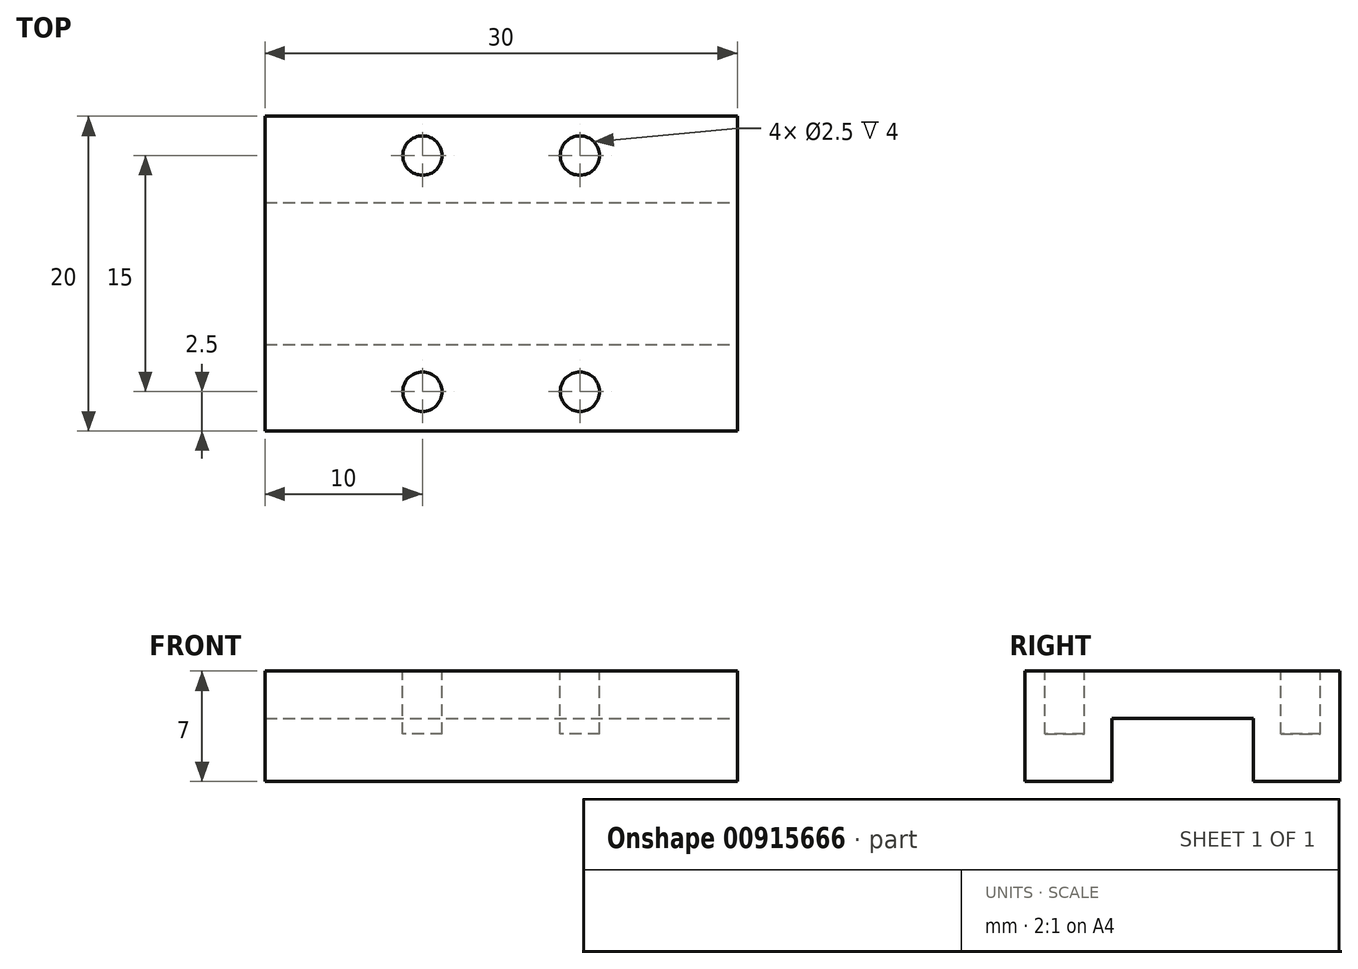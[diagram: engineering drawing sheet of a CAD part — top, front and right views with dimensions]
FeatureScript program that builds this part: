
annotation { "Feature Type Name" : "Feature", "Feature Type Description" : "" }
export const myFeature = defineFeature(function(context is Context, id is Id, definition is map)
    precondition{}
    {
        {
            var Q0;
            Q0=qCreatedBy(makeId("Top.planeOp"),FACE);
            var sketch = newSketch(context, id + "F0", { "sketchPlane" : qUnion([Q0])});
            skLineSegment(sketch, "E0.bottom", {"start": v(-15, 10) * mm, "end": v(15, 10) * mm});
            skLineSegment(sketch, "E0.top", {"start": v(-15, -10) * mm, "end": v(15, -10) * mm});
            skLineSegment(sketch, "E0.left", {"start": v(-15, 10) * mm, "end": v(-15, -10) * mm});
            skLineSegment(sketch, "E0.right", {"start": v(15, 10) * mm, "end": v(15, -10) * mm});
            skSolve(sketch);
        }
        {
            var Q0;
            Q0 = qSketchRegion(id + "F0", true);
            extrude(context, id + "F1", {"entities" : qUnion([Q0]), "depth" : 7 * mm, "offsetDistance" : 25 * mm});
        }
        {
            var Q0;
            Q0=makeQuery(id+"F1.opExtrude","CAP_FACE",FACE,{"disambiguationData":[OSD([sQuery(id+"F0.wireOp",EDGE,"E0.bottom"),sQuery(id+"F0.wireOp",EDGE,"E0.top"),sQuery(id+"F0.wireOp",EDGE,"E0.left"),sQuery(id+"F0.wireOp",EDGE,"E0.right")])],"isStart":false});
            var sketch = newSketch(context, id + "F2", { "sketchPlane" : qUnion([Q0])});
            skLineSegment(sketch, "E1.bottom", {"start": v(-5, 7.5) * mm, "end": v(5, 7.5) * mm, "construction": true});
            skLineSegment(sketch, "E1.top", {"start": v(-5, -7.5) * mm, "end": v(5, -7.5) * mm, "construction": true});
            skLineSegment(sketch, "E1.left", {"start": v(-5, 7.5) * mm, "end": v(-5, -7.5) * mm, "construction": true});
            skLineSegment(sketch, "E1.right", {"start": v(5, 7.5) * mm, "end": v(5, -7.5) * mm, "construction": true});
            skCircle(sketch, "E2", {"center": v(5, 7.5) * mm, "radius": 1.25 * mm});
            skCircle(sketch, "E3", {"center": v(-5, 7.5) * mm, "radius": 1.25 * mm});
            skCircle(sketch, "E4", {"center": v(-5, -7.5) * mm, "radius": 1.25 * mm});
            skCircle(sketch, "E5", {"center": v(5, -7.5) * mm, "radius": 1.25 * mm});
            skSolve(sketch);
        }
        {
            var Q0;
            Q0 = qSketchRegion(id + "F2", true);
            extrude(context, id + "F3", {"entities" : qUnion([Q0]), "operationType" : NewBodyOperationType.REMOVE, "oppositeDirection" : true, "depth" : 4 * mm, "offsetDistance" : 25 * mm});
        }
        {
            var Q0;
            Q0=makeQuery(id+"F1.opExtrude","CAP_FACE",FACE,{"disambiguationData":[OSD([sQuery(id+"F0.wireOp",EDGE,"E0.bottom"),sQuery(id+"F0.wireOp",EDGE,"E0.top"),sQuery(id+"F0.wireOp",EDGE,"E0.left"),sQuery(id+"F0.wireOp",EDGE,"E0.right")])],"isStart":true});
            var sketch = newSketch(context, id + "F4", { "sketchPlane" : qUnion([Q0])});
            skLineSegment(sketch, "E6.bottom", {"start": v(-15, 4.5) * mm, "end": v(15, 4.5) * mm});
            skLineSegment(sketch, "E6.top", {"start": v(-15, -4.5) * mm, "end": v(15, -4.5) * mm});
            skLineSegment(sketch, "E6.left", {"start": v(-15, 4.5) * mm, "end": v(-15, -4.5) * mm});
            skLineSegment(sketch, "E6.right", {"start": v(15, 4.5) * mm, "end": v(15, -4.5) * mm});
            skSolve(sketch);
        }
        {
            var Q0;
            Q0 = qSketchRegion(id + "F4", true);
            extrude(context, id + "F5", {"entities" : qUnion([Q0]), "operationType" : NewBodyOperationType.REMOVE, "oppositeDirection" : true, "depth" : 4 * mm, "offsetDistance" : 25 * mm});
        }
    });
